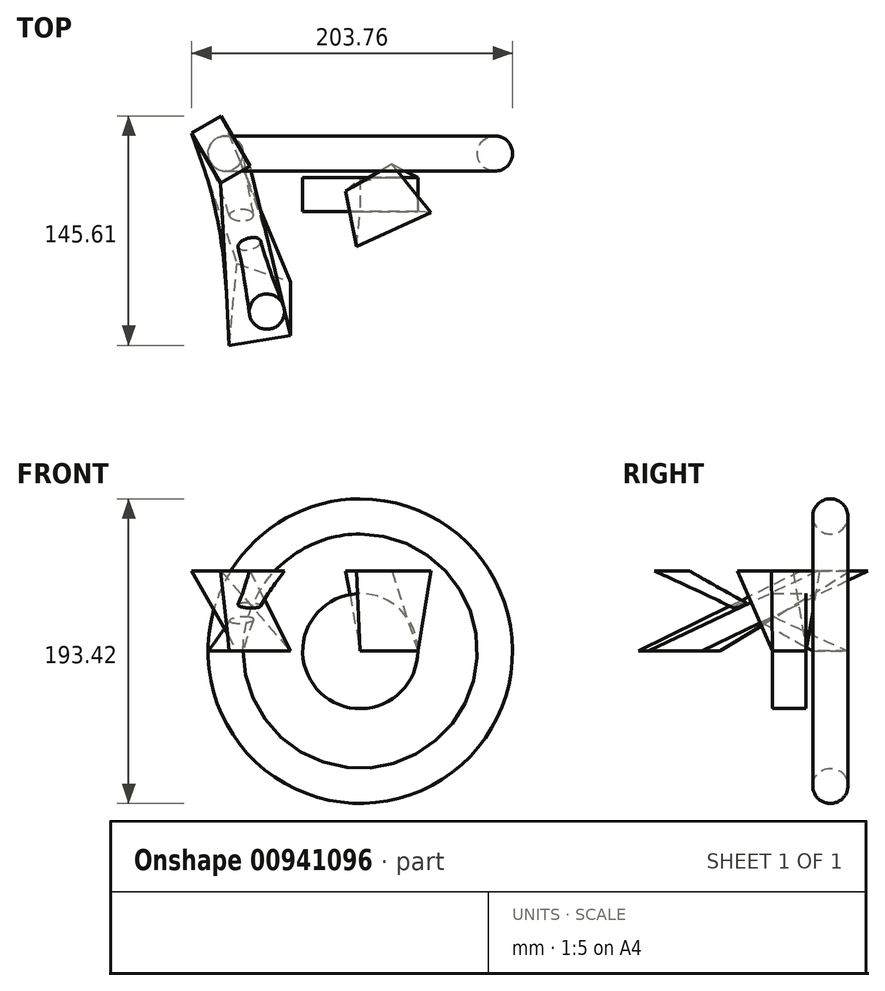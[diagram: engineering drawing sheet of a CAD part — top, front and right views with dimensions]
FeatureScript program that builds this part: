
annotation { "Feature Type Name" : "Feature", "Feature Type Description" : "" }
export const myFeature = defineFeature(function(context is Context, id is Id, definition is map)
    precondition{}
    {
        {
            var Q0;
            Q0=qCreatedBy(makeId("Top.planeOp"),FACE);
            var sketch = newSketch(context, id + "F0", { "sketchPlane" : qUnion([Q0])});
            skCircle(sketch, "E0", {"center": v(-62.28, 52.52) * mm, "radius": 11.18 * mm});
            skLineSegment(sketch, "E1.bottom", {"start": v(23.25, 37.16) * mm, "end": v(59.79, 37.16) * mm});
            skLineSegment(sketch, "E1.top", {"start": v(23.25, 15.57) * mm, "end": v(59.79, 15.57) * mm});
            skLineSegment(sketch, "E1.left", {"start": v(23.25, 37.16) * mm, "end": v(23.25, 15.57) * mm});
            skLineSegment(sketch, "E1.right", {"start": v(59.79, 37.16) * mm, "end": v(59.79, 15.57) * mm});
            skLineSegment(sketch, "E2", {"start": v(-55, -17.45) * mm, "end": v(-20.95, -29.08) * mm});
            skLineSegment(sketch, "E3", {"start": v(-20.95, -29.08) * mm, "end": v(-20.95, -63.13) * mm});
            skLineSegment(sketch, "E4", {"start": v(-20.95, -63.13) * mm, "end": v(-59.98, -69.35) * mm});
            skLineSegment(sketch, "E5", {"start": v(-59.98, -69.35) * mm, "end": v(-55, -17.45) * mm});
            skLineSegment(sketch, "E6", {"start": v(-82.91, 71.7) * mm, "end": v(-82.91, 30.26) * mm, "construction": true});
            skSolve(sketch);
        }
        {
            var Q0;
            Q0=qCreatedBy(makeId("Top.planeOp"),FACE);
            cPlane(context, id + "F1", {"entities" : qUnion([Q0]), "cplaneType" : CPlaneType.OFFSET, "offset" : 50.8 * mm, "width" : 152.4 * mm, "height" : 152.4 * mm});
        }
        {
            var Q0;
            Q0=qCreatedBy(id+"F1.planeOp",FACE);
            var sketch = newSketch(context, id + "F2", { "sketchPlane" : qUnion([Q0])});
            skCircle(sketch, "E7.0", {"center": v(-36.07, -47.94) * mm, "radius": 11.18 * mm});
            skLineSegment(sketch, "E7.1.0", {"start": v(-65.53, 33.82) * mm, "end": v(-46.83, 44.61) * mm});
            skLineSegment(sketch, "E7.1.1", {"start": v(-46.83, 44.61) * mm, "end": v(-65.1, 76.26) * mm});
            skLineSegment(sketch, "E7.1.2", {"start": v(-65.1, 76.26) * mm, "end": v(-83.8, 65.46) * mm});
            skLineSegment(sketch, "E7.1.3", {"start": v(-83.8, 65.46) * mm, "end": v(-65.53, 33.82) * mm});
            skLineSegment(sketch, "E7.2.0", {"start": v(20.9, -6.64) * mm, "end": v(68.33, 15) * mm});
            skLineSegment(sketch, "E7.2.1", {"start": v(68.33, 15) * mm, "end": v(43.42, 45.68) * mm});
            skLineSegment(sketch, "E7.2.2", {"start": v(43.42, 45.68) * mm, "end": v(13.94, 28.66) * mm});
            skLineSegment(sketch, "E7.2.3", {"start": v(13.94, 28.66) * mm, "end": v(20.9, -6.64) * mm});
            skSolve(sketch);
        }
        {
            var Q0;
            Q0=makeQuery(id+"F2.imprint","IMPRINT",FACE,{"disambiguationData":[TD([[makeQuery(id+"F2.imprint","IMPRINT",EDGE,{"derivedFrom":sQuery(id+"F2.wireOp",EDGE,"E7.2.0")}),1.0]])]});
            var Q1;
            Q1=makeQuery(id+"F0.imprint","IMPRINT",FACE,{"disambiguationData":[TD([[makeQuery(id+"F0.imprint","IMPRINT",EDGE,{"derivedFrom":sQuery(id+"F0.wireOp",EDGE,"E1.bottom")}),-1.0]])]});
            loft(context, id + "F3", {"sheetProfilesArray" : [{ "sheetProfileEntities" : qUnion([Q0]) }, { "sheetProfileEntities" : qUnion([Q1]) }]});
        }
        {
            var Q0;
            Q0=makeQuery(id+"F0.imprint","IMPRINT",FACE,{"disambiguationData":[TD([[makeQuery(id+"F0.imprint","IMPRINT",EDGE,{"derivedFrom":sQuery(id+"F0.wireOp",EDGE,"E0")}),1.0]])]});
            var Q1;
            Q1=makeQuery(id+"F2.imprint","IMPRINT",FACE,{"disambiguationData":[TD([[makeQuery(id+"F2.imprint","IMPRINT",EDGE,{"derivedFrom":sQuery(id+"F2.wireOp",EDGE,"E7.0")}),1.0]])]});
            loft(context, id + "F4", {"sheetProfilesArray" : [{ "sheetProfileEntities" : qUnion([Q0]) }, { "sheetProfileEntities" : qUnion([Q1]) }]});
        }
        {
            var Q1;
            Q1=makeQuery(id+"F2.imprint","IMPRINT",FACE,{"disambiguationData":[TD([[makeQuery(id+"F2.imprint","IMPRINT",EDGE,{"derivedFrom":sQuery(id+"F2.wireOp",EDGE,"E7.1.0")}),1.0]])]});
            var Q2;
            Q2=makeQuery(id+"F0.imprint","IMPRINT",FACE,{"disambiguationData":[TD([[makeQuery(id+"F0.imprint","IMPRINT",EDGE,{"derivedFrom":sQuery(id+"F0.wireOp",EDGE,"E2")}),-1.0]])]});
            loft(context, id + "F5", {"operationType" : NewBodyOperationType.ADD, "sheetProfilesArray" : [{ "sheetProfileEntities" : qUnion([Q1]) }, { "sheetProfileEntities" : qUnion([Q2]) }]});
        }
        {
            var Q0;
            Q0=makeQuery(id+"F0.imprint","IMPRINT",FACE,{"disambiguationData":[TD([[makeQuery(id+"F0.imprint","IMPRINT",EDGE,{"derivedFrom":sQuery(id+"F0.wireOp",EDGE,"E0")}),1.0]])]});
            var Q1;
            Q1=makeQuery(id+"F0.imprint","IMPRINT",FACE,{"disambiguationData":[TD([[makeQuery(id+"F0.imprint","IMPRINT",EDGE,{"derivedFrom":sQuery(id+"F0.wireOp",EDGE,"E1.bottom")}),-1.0]])]});
            var Q2;
            Q2=sQuery(id+"F0.wireOp",EDGE,"E1.left");
            revolve(context, id + "F6", {"surfaceOperationType" : NewSurfaceOperationType.NEW, "entities" : qUnion([Q0, Q1]), "axis" : qUnion([Q2]), "revolveType" : RevolveType.FULL});
        }
    });
